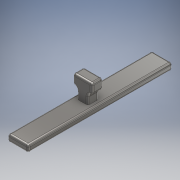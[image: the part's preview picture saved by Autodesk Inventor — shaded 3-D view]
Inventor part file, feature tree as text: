
AUTODESK INVENTOR PART (.ipt)
format: ipt  version: 2018 (Build 220112000, 112)  size: 178,688 bytes
history: native  units: mm
features: extrude x4, sketch x4, fillet x3
ambient origin geometry x8: Origin, YZ Plane, XZ Plane, XY Plane, X Axis, Y Axis, Z Axis, Center Point
bodies: Solid1 (feature_tree)
feature tree (11):
  extrude  "Extrusion1"  Depth=5.0mm
  extrude  "Extrusion2"  Depth=8.0mm
  extrude  "Extrusion3"  Depth=55.0mm
  extrude  "Extrusion4"  Depth=1.5mm
  fillet  "Fillet1"  Radius=8.0mm
  fillet  "Fillet2"  Radius=3.0mm
  fillet  "Fillet3"  Radius=7.0mm
  sketch  "Sketch1"  dims[d2=15.0mm d3=5.0mm]
  sketch  "Sketch2"  dims[d4=105.0mm d5=0.0mm d6=8.0mm]
  sketch  "Sketch3"  dims[d7=8.0mm d8=55.0mm]
  sketch  "Sketch4"  dims[d9=15.0mm d10=0.0mm d11=7.0mm d12=8.0mm d13=3.0mm d14=0.0mm d15=7.0mm d16=8.0mm d17=3.0mm d18=0.0mm d19=3.0mm d20=1.5mm d21=1.5mm]
